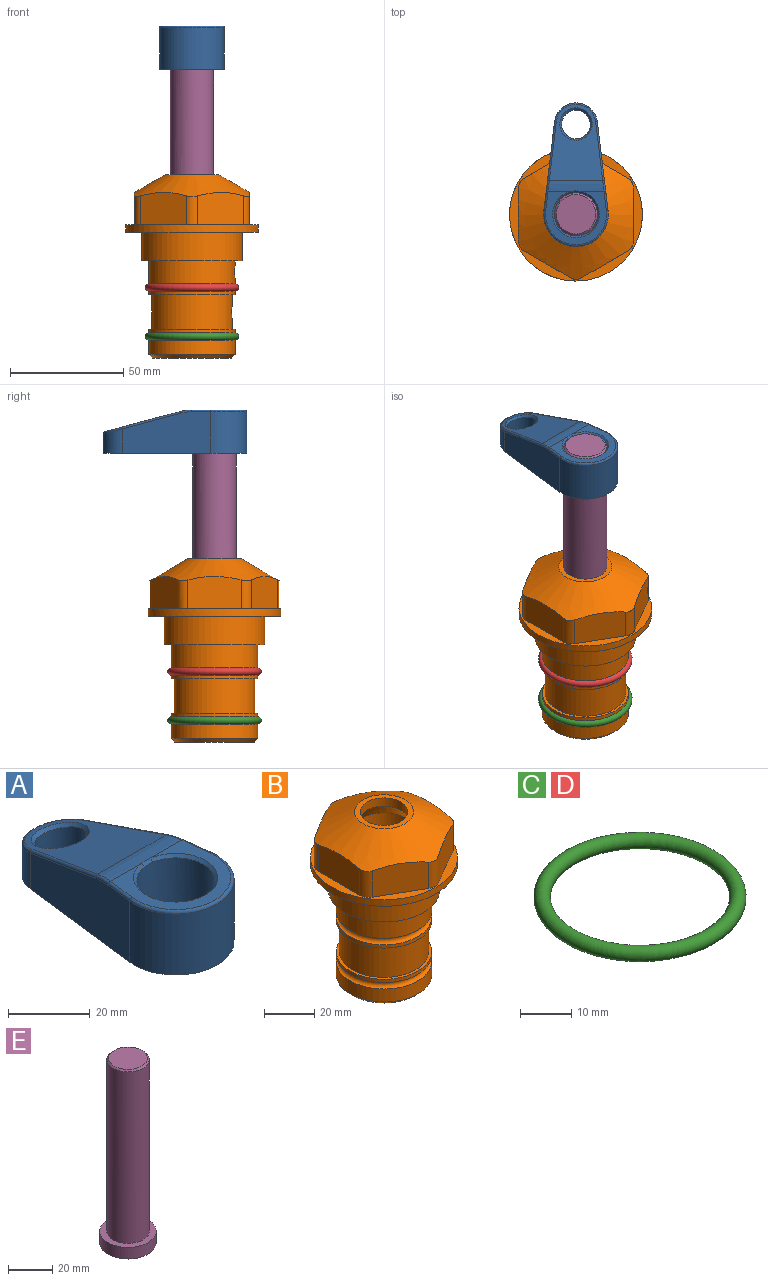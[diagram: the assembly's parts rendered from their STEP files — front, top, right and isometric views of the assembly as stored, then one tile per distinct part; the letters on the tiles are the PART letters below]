
ASSEMBLY  parts=5 mates=4
PART A: 31 faces, bbox 31.7x65.5x19.8 mm
  f0: plane 39.12x18.26mm, normal (0.99,0.12,0), area 612.2mm2, adj f1,f4,f7,f11,f13,f15
  f1: cylinder r=9.53mm len=18.91mm, axis (0,0,-1), area 296.1mm2, adj f0,f2,f7,f17
  f2: plane 39.12x18.26mm, normal (-0.99,0.12,0), area 612.2mm2, adj f1,f4,f7,f12,f14,f16
  f3: cylinder r=6.35mm len=12.7mm, axis (0,0,-1), area 362.4mm2, adj f7,f18
  f4: cylinder r=14.29mm len=28.58mm, axis (0,0,-1), area 882.2mm2, adj f0,f2,f7,f10
  f5: cylinder r=9.53mm len=19.05mm, axis (0,0,-1), area 1092.6mm2, adj f7,f19,f20
  f6: plane 26.99x23.69mm, normal (0,0,1), area 216.2mm2, adj f9,f10,f11,f12,f19
  f7: plane 63.5x28.58mm, normal (0,0,-1), area 661.8mm2, adj f0,f1,f2,f3,f4,f5,f22,f23
  f8: plane 33.52x23.6mm, normal (0,0.26,0.97), area 486mm2, adj f9,f15,f16,f17,f18
  f9: cylinder r=19.05mm len=24.72mm, axis (1,0,0), area 120.4mm2, adj f6,f8,f13,f14,f20
  f10: torus R=13.49mm, axis (0,0,1), area 59mm2, adj f4,f6,f11,f12
  f11: cylinder r=0.79mm len=8.67mm, axis (0.12,-0.99,0), area 10.8mm2, adj f0,f6,f10,f13
  f12: cylinder r=0.79mm len=8.67mm, axis (0.12,0.99,0), area 10.8mm2, adj f2,f6,f10,f14
  f13: bspline ~4.95x1.42mm, area 6.1mm2, adj f0,f9,f11,f15
  f14: bspline ~4.95x1.42mm, area 6.1mm2, adj f2,f9,f12,f16
  f15: cylinder r=0.79mm len=25.95mm, axis (0.12,-0.96,0.26), area 32.9mm2, adj f0,f8,f13,f17
  f16: cylinder r=0.79mm len=25.95mm, axis (0.12,0.96,-0.26), area 32.9mm2, adj f2,f8,f14,f17
  f17: bspline ~18.91x8.38mm, area 30mm2, adj f1,f8,f15,f16
  f18: bspline ~14.29x14.29mm, area 48.3mm2, adj f3,f8
  f19: cone r=9.53mm half-angle=45deg, axis (0,0,1), area 66.5mm2, adj f5,f6,f20
  f20: bspline ~3.22x0.96mm, area 3.5mm2, adj f5,f9,f19
  f21: plane 2.75x2.72mm, normal (0,0,-1), area 2.9mm2, adj f23,f25,f28
  f22: plane 23.05x15.88mm, normal (-0.99,-0.12,0), area 323.6mm2, adj f7,f25,f26,f27,f28,f29
  f23: plane 23.05x15.88mm, normal (0.99,-0.12,0), area 323.6mm2, adj f7,f21,f25,f27,f28,f30
  f24: cylinder r=9.53mm len=10.69mm, axis (0,0,-1), area 114.7mm2, adj f7,f27,f29,f30
  f25: cylinder r=12.7mm len=20.59mm, axis (0,0,-1), area 381.1mm2, adj f7,f21,f22,f23,f26,f28
  f26: plane 2.75x2.72mm, normal (0,0,-1), area 2.9mm2, adj f22,f25,f28
  f27: plane 19.72x18.37mm, normal (0,-0.26,-0.97), area 291.8mm2, adj f22,f23,f24,f28,f29,f30
  f28: cylinder r=15.88mm len=19.92mm, axis (1,0,0), area 54.8mm2, adj f21,f22,f23,f25,f26,f27
  f29: cylinder r=1.59mm len=11mm, axis (0,0,-1), area 34.7mm2, adj f7,f22,f24,f27
  f30: cylinder r=1.59mm len=11mm, axis (0,0,-1), area 34.7mm2, adj f7,f23,f24,f27
PART B: 36 faces, bbox 58.7x58.7x81 mm
  f0: cylinder r=17.78mm len=35.56mm, axis (0,0,1), area 1670.8mm2, adj f23,f24,f31
  f1: cylinder r=19.05mm len=38.1mm, axis (0,0,1), area 1191.9mm2, adj f26,f27,f30
  f2: plane 58.66x58.66mm, normal (0,0,-1), area 1150.6mm2, adj f3,f28
  f3: cylinder r=29.33mm len=58.66mm, axis (0,0,-1), area 585.1mm2, adj f2,f4
  f4: plane 58.66x58.66mm, normal (0,0,1), area 475.9mm2, adj f3,f5,f6,f7,f8,f9,f10,f11
  f5: plane 20.32x14.34mm, normal (-0.5,0.87,0), area 324.4mm2, adj f4,f15,f16,f17
  f6: plane 20.32x14.34mm, normal (0.5,0.87,0), area 324.4mm2, adj f4,f14,f15,f17
  f7: plane 23.48x14.34mm, normal (1,0,0), area 324.4mm2, adj f4,f13,f14,f17
  f8: plane 20.32x14.34mm, normal (0.5,-0.87,0), area 324.4mm2, adj f4,f12,f13,f17
  f9: plane 20.32x14.34mm, normal (-0.5,-0.87,0), area 324.4mm2, adj f4,f11,f12,f17
  f10: plane 23.48x14.34mm, normal (-1,0,0), area 324.4mm2, adj f4,f11,f16,f17
  f11: cylinder r=5.08mm len=12.85mm, axis (0,0,-1), area 67.2mm2, adj f4,f9,f10,f17
  f12: cylinder r=5.08mm len=12.85mm, axis (0,0,-1), area 67.2mm2, adj f4,f8,f9,f17
  f13: cylinder r=5.08mm len=12.85mm, axis (0,0,-1), area 67.2mm2, adj f4,f7,f8,f17
  f14: cylinder r=5.08mm len=12.85mm, axis (0,0,-1), area 67.2mm2, adj f4,f6,f7,f17
  f15: cylinder r=5.08mm len=12.85mm, axis (0,0,-1), area 67.2mm2, adj f4,f5,f6,f17
  f16: cylinder r=5.08mm len=12.85mm, axis (0,0,-1), area 67.2mm2, adj f4,f5,f10,f17
  f17: cone r=11.73mm half-angle=60deg, axis (0,0,-1), area 2071.8mm2, adj f5,f6,f7,f8,f9,f10,f11,f12
  f18: plane 23.46x23.46mm, normal (0,0,1), area 147.4mm2, adj f17,f35
  f19: plane 34.93x34.93mm, normal (0,0,-1), area 958mm2, adj f29
  f20: cylinder r=19.05mm len=38.1mm, axis (0,0,1), area 760.1mm2, adj f21,f29
  f21: torus R=19.05mm, axis (0,0,1), area 565.3mm2, adj f20,f22
  f22: cylinder r=19.05mm len=38.1mm, axis (0,0,1), area 190mm2, adj f21,f23
  f23: plane 38.1x38.1mm, normal (0,0,1), area 146.9mm2, adj f0,f22
  f24: plane 38.1x38.1mm, normal (0,0,-1), area 146.9mm2, adj f0,f25
  f25: cylinder r=19.05mm len=38.1mm, axis (0,0,1), area 190mm2, adj f24,f26
  f26: torus R=19.05mm, axis (0,0,1), area 565.3mm2, adj f1,f25
  f27: plane 44.45x44.45mm, normal (0,0,-1), area 411.7mm2, adj f1,f28
  f28: cylinder r=22.23mm len=44.45mm, axis (0,0,1), area 1773.5mm2, adj f2,f27
  f29: cone r=19.05mm half-angle=45deg, axis (0,0,1), area 257.5mm2, adj f19,f20
  f30: cylinder r=3.17mm len=6.75mm, axis (-1,0,0), area 128mm2, adj f1,f33
  f31: cylinder r=3.17mm len=6.35mm, axis (-1,0,0), area 102.5mm2, adj f0,f33
  f32: plane 25.4x25.4mm, normal (0,0,1), area 506.7mm2, adj f33
  f33: cylinder r=12.7mm len=66.42mm, axis (0,0,-1), area 5236.2mm2, adj f30,f31,f32,f34
  f34: cone r=9.53mm half-angle=30deg, axis (0,0,-1), area 443.4mm2, adj f33,f35
  f35: cylinder r=9.53mm len=19.05mm, axis (0,0,-1), area 240.9mm2, adj f18,f34
PART C: 1 faces, bbox 44.7x44.7x3.2 mm
  f0: torus R=19.05mm, axis (0,0,1), area 1193.9mm2
PART D: same geometry as C
PART E: 6 faces, bbox 25.4x25.4x101.6 mm
  f0: plane 17.46x17.46mm, normal (0,0,1), area 239.5mm2, adj f5
  f1: plane 25.4x25.4mm, normal (0,0,-1), area 506.7mm2, adj f2
  f2: cylinder r=12.7mm len=25.4mm, axis (0,0,1), area 506.7mm2, adj f1,f3
  f3: plane 25.4x25.4mm, normal (0,0,1), area 221.7mm2, adj f2,f4
  f4: cylinder r=9.53mm len=94.46mm, axis (0,0,1), area 5653mm2, adj f3,f5
  f5: cone r=8.73mm half-angle=45deg, axis (0,0,-1), area 64.4mm2, adj f0,f4
PLACE A t=(0,0,27.55)mm
PLACE B at identity fixed
PLACE C t=(0,0,-21.59)mm
PLACE D at identity
PLACE E t=(0,0,27.55)mm
MATE slider E.f2 <-> B.f0  axis (0,0,-1) through (0,0,-10.55)mm
MATE fastened B.f0 <-> D.f0  axis (0,0,1) through (0,0,-24.51)mm
MATE fastened B.f0 <-> C.f0  axis (0,0,1) through (0,0,-46.1)mm
MATE fastened E.f2 <-> A.f4  axis (0,0,1) through (0,0,91.05)mm
